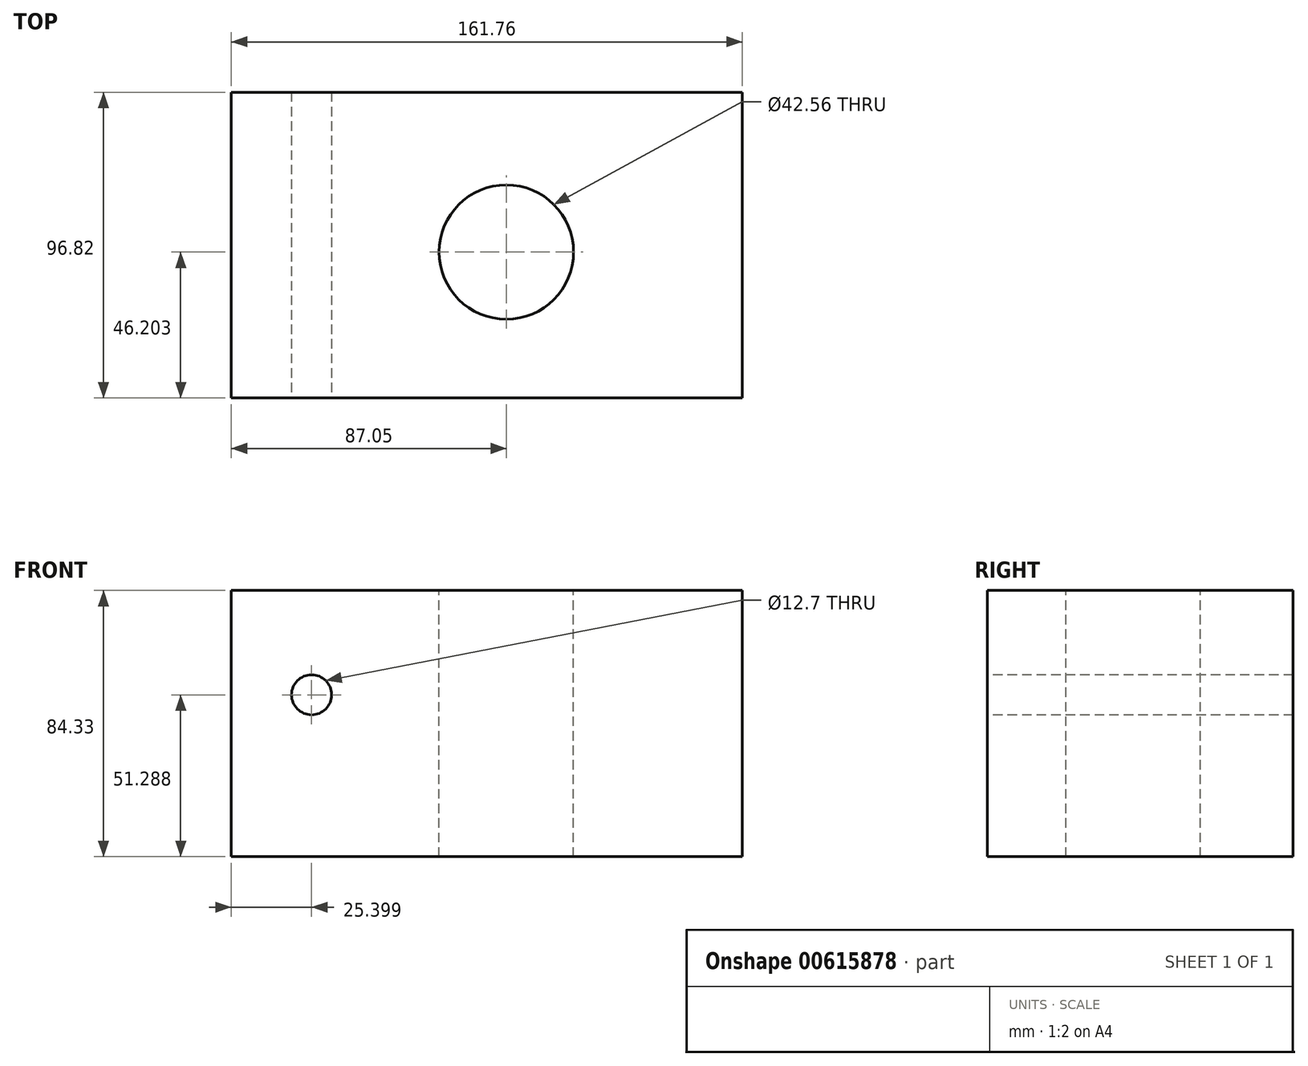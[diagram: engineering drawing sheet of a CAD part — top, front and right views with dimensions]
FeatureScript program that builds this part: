
annotation { "Feature Type Name" : "Feature", "Feature Type Description" : "" }
export const myFeature = defineFeature(function(context is Context, id is Id, definition is map)
    precondition{}
    {
        {
            var Q0;
            Q0=qCreatedBy(makeId("Top.planeOp"),FACE);
            var sketch = newSketch(context, id + "F0", { "sketchPlane" : qUnion([Q0])});
            skLineSegment(sketch, "E0.bottom", {"start": v(-63.11, -42.12) * mm, "end": v(98.65, -42.12) * mm});
            skLineSegment(sketch, "E0.top", {"start": v(-63.11, 54.7) * mm, "end": v(98.65, 54.7) * mm});
            skLineSegment(sketch, "E0.left", {"start": v(-63.11, -42.12) * mm, "end": v(-63.11, 54.7) * mm});
            skLineSegment(sketch, "E0.right", {"start": v(98.65, -42.12) * mm, "end": v(98.65, 54.7) * mm});
            skSolve(sketch);
        }
        {
            var Q0;
            Q0 = qSketchRegion(id + "F0", true);
            extrude(context, id + "F1", {"entities" : qUnion([Q0]), "depth" : 84.33 * mm, "offsetDistance" : 25.4 * mm});
        }
        {
            var Q0;
            Q0=makeQuery(id+"F1.opExtrude","CAP_FACE",FACE,{"disambiguationData":[OSD([sQuery(id+"F0.wireOp",EDGE,"E0.bottom"),sQuery(id+"F0.wireOp",EDGE,"E0.top"),sQuery(id+"F0.wireOp",EDGE,"E0.left"),sQuery(id+"F0.wireOp",EDGE,"E0.right")])],"isStart":false});
            var sketch = newSketch(context, id + "F2", { "sketchPlane" : qUnion([Q0])});
            skCircle(sketch, "E1", {"center": v(23.94, 4.08) * mm, "radius": 21.28 * mm});
            skSolve(sketch);
        }
        {
            var Q0;
            Q0 = qSketchRegion(id + "F2", true);
            extrude(context, id + "F3", {"entities" : qUnion([Q0]), "operationType" : NewBodyOperationType.REMOVE, "endBound" : BoundingType.THROUGH_ALL, "oppositeDirection" : true, "depth" : 25.4 * mm, "offsetDistance" : 25.4 * mm});
        }
        {
            var Q0;
            Q0=makeQuery(id+"F1.opExtrude","SWEPT_FACE",FACE,{"disambiguationData":[OSD([sQuery(id+"F0.wireOp",EDGE,"E0.bottom")])]});
            var sketch = newSketch(context, id + "F4", { "sketchPlane" : qUnion([Q0])});
            skCircle(sketch, "E2", {"center": v(-37.71, 51.29) * mm, "radius": 6.35 * mm});
            skSolve(sketch);
        }
        {
            var Q0;
            Q0 = qSketchRegion(id + "F4", true);
            extrude(context, id + "F5", {"entities" : qUnion([Q0]), "operationType" : NewBodyOperationType.REMOVE, "endBound" : BoundingType.THROUGH_ALL, "oppositeDirection" : true, "depth" : 25.4 * mm, "offsetDistance" : 25.4 * mm});
        }
    });
